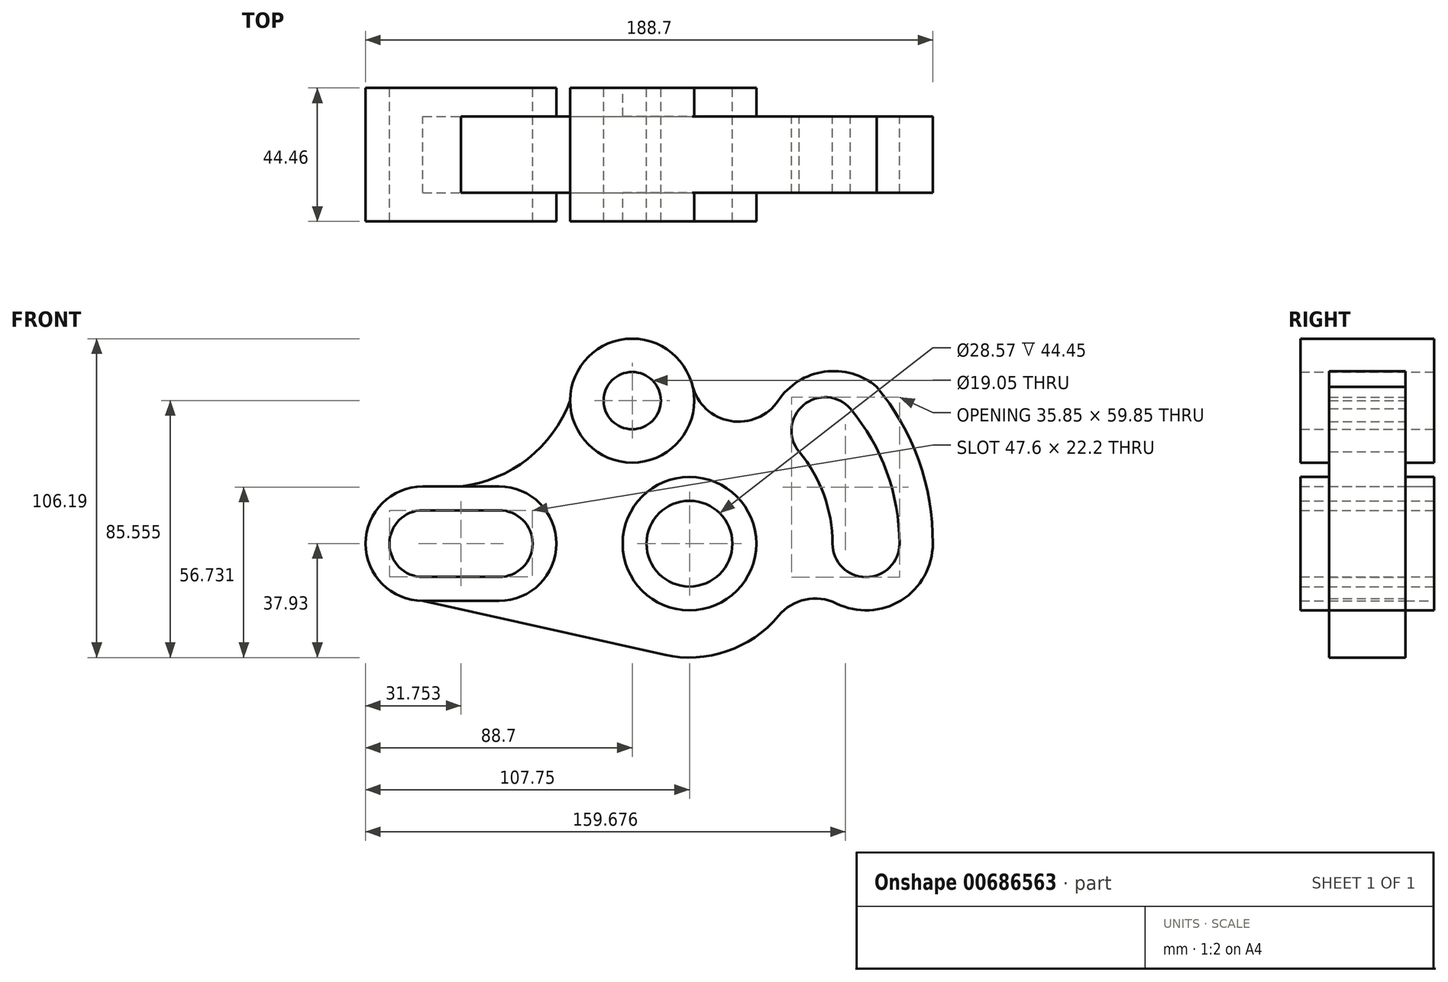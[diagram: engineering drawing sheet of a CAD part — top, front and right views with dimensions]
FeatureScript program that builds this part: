
annotation { "Feature Type Name" : "Feature", "Feature Type Description" : "" }
export const myFeature = defineFeature(function(context is Context, id is Id, definition is map)
    precondition{}
    {
        {
            var Q0;
            Q0=qCreatedBy(makeId("Front.planeOp"),FACE);
            var sketch = newSketch(context, id + "F0", { "sketchPlane" : qUnion([Q0])});
            skCircle(sketch, "E0", {"center": v(0, 0) * mm, "radius": 14.29 * mm});
            skCircle(sketch, "E1", {"center": v(0, 0) * mm, "radius": 22.23 * mm});
            skCircle(sketch, "E2", {"center": v(-19.05, 47.62) * mm, "radius": 9.53 * mm});
            skCircle(sketch, "E3", {"center": v(-19.05, 47.62) * mm, "radius": 20.64 * mm});
            skArc(sketch, "E4", {"start": v(-88.7, 11.1) * mm, "mid": v(-99.8, 0) * mm, "end": v(-88.7, -11.1) * mm});
            skArc(sketch, "E5", {"start": v(-63.3, -11.1) * mm, "mid": v(-52.2, 0) * mm, "end": v(-63.3, 11.1) * mm});
            skLineSegment(sketch, "E6", {"start": v(-88.7, 11.1) * mm, "end": v(-63.3, 11.1) * mm});
            skLineSegment(sketch, "E7", {"start": v(-88.7, -11.1) * mm, "end": v(-63.3, -11.1) * mm});
            skArc(sketch, "E8", {"start": v(48.87, -19.92) * mm, "mid": v(70.45, -18.88) * mm, "end": v(80.95, 0) * mm});
            skLineSegment(sketch, "E9", {"start": v(0, 0) * mm, "end": v(17.03, 14.29) * mm, "construction": true});
            skLineSegment(sketch, "E10", {"start": v(0, 0) * mm, "end": v(22.23, 0) * mm, "construction": true});
            skArc(sketch, "E11.filletArc", {"start": v(48.87, -19.92) * mm, "mid": v(38.53, -18.62) * mm, "end": v(29.62, -24.02) * mm});
            skArc(sketch, "E12", {"start": v(47.6, 0) * mm, "mid": v(58.72, -11.13) * mm, "end": v(69.85, 0) * mm});
            skArc(sketch, "E13", {"start": v(53.5, 44.9) * mm, "mid": v(37.93, 46.16) * mm, "end": v(36.46, 30.6) * mm});
            skArc(sketch, "E14", {"start": v(62.28, 52.26) * mm, "mid": v(44.88, 57.24) * mm, "end": v(29.55, 47.63) * mm});
            skLineSegment(sketch, "E15", {"start": v(0, 0) * mm, "end": v(-125.57, 0) * mm, "construction": true});
            skLineSegment(sketch, "E16", {"start": v(0, 0) * mm, "end": v(0, 0.55) * mm, "construction": true});
            skArc(sketch, "E17", {"start": v(36.46, 30.6) * mm, "mid": v(44.73, 16.28) * mm, "end": v(47.6, 0) * mm});
            skArc(sketch, "E18", {"start": v(53.5, 44.9) * mm, "mid": v(65.64, 23.9) * mm, "end": v(69.85, 0) * mm});
            skArc(sketch, "E19", {"start": v(62.28, 52.26) * mm, "mid": v(76.23, 27.78) * mm, "end": v(80.95, 0) * mm});
            skLineSegment(sketch, "E20.trimOffspring", {"start": v(0, 14.29) * mm, "end": v(0, 22.23) * mm, "construction": true});
            skLineSegment(sketch, "E21.trimOffspring", {"start": v(0, 0.55) * mm, "end": v(0, 0) * mm, "construction": true});
            skLineSegment(sketch, "E22.trimOffspring", {"start": v(0, -14.29) * mm, "end": v(0, -22.23) * mm, "construction": true});
            skArc(sketch, "E23", {"start": v(-63.3, -19.05) * mm, "mid": v(-44.25, 0) * mm, "end": v(-63.3, 19.05) * mm});
            skLineSegment(sketch, "E24", {"start": v(-88.7, 19.05) * mm, "end": v(-63.3, 19.05) * mm});
            skLineSegment(sketch, "E25", {"start": v(-88.7, -19.05) * mm, "end": v(-63.3, -19.05) * mm});
            skLineSegment(sketch, "E26", {"start": v(-76, 0) * mm, "end": v(-76, 19.05) * mm, "construction": true});
            skPoint(sketch, "E26.startSnap0", {"position": v(-76, 11.1) * mm});
            skPoint(sketch, "E26.endSnap0", {"position": v(-76, 19.05) * mm});
            skArc(sketch, "E27.MirrorCS", {"start": v(-88.7, -19.05) * mm, "mid": v(-107.75, 0) * mm, "end": v(-88.7, 19.05) * mm});
            skArc(sketch, "E28", {"start": v(-76, 19.05) * mm, "mid": v(-53.84, 28.25) * mm, "end": v(-39.69, 47.62) * mm});
            skArc(sketch, "E29", {"start": v(-8.4, -37) * mm, "mid": v(12.44, -35.86) * mm, "end": v(29.62, -24.02) * mm});
            skLineSegment(sketch, "E30", {"start": v(-88.7, -19.05) * mm, "end": v(-8.4, -37) * mm});
            skArc(sketch, "E31", {"start": v(0.97, 52.63) * mm, "mid": v(13.64, 40.84) * mm, "end": v(29.55, 47.62) * mm});
            skPoint(sketch, "E32.orphan", {"position": v(-76, 37.27) * mm});
            skLineSegment(sketch, "E33.trimOffspring", {"start": v(62.28, 52.26) * mm, "end": v(90.16, 75.27) * mm, "construction": true});
            skLineSegment(sketch, "E34.trimOffspring", {"start": v(80.95, 0) * mm, "end": v(110.19, 0) * mm, "construction": true});
            skSolve(sketch);
        }
        {
            var Q0;
            Q0=makeQuery(id+"F0.imprint","IMPRINT",FACE,{"disambiguationData":[TD([[makeQuery(id+"F0.imprint","IMPRINT",EDGE,{"derivedFrom":sQuery(id+"F0.wireOp",EDGE,"E1")}),-1.0]])]});
            extrude(context, id + "F1", {"entities" : qUnion([Q0]), "endBound" : BoundingType.SYMMETRIC, "depth" : 25.4 * mm, "offsetDistance" : 25.4 * mm});
        }
        {
            var Q0;
            Q0=makeQuery(id+"F0.imprint","IMPRINT",FACE,{"disambiguationData":[TD([[makeQuery(id+"F0.imprint","IMPRINT",EDGE,{"derivedFrom":sQuery(id+"F0.wireOp",EDGE,"E0")}),-1.0]])]});
            var Q1;
            Q1=makeQuery(id+"F0.imprint","IMPRINT",FACE,{"disambiguationData":[TD([[makeQuery(id+"F0.imprint","IMPRINT",EDGE,{"derivedFrom":sQuery(id+"F0.wireOp",EDGE,"E4")}),-1.0]])]});
            var Q2;
            Q2=makeQuery(id+"F0.imprint","IMPRINT",FACE,{"disambiguationData":[TD([[makeQuery(id+"F0.imprint","IMPRINT",EDGE,{"derivedFrom":sQuery(id+"F0.wireOp",EDGE,"E2")}),-1.0]])]});
            extrude(context, id + "F2", {"entities" : qUnion([Q0, Q1, Q2]), "operationType" : NewBodyOperationType.ADD, "endBound" : BoundingType.SYMMETRIC, "depth" : 44.45 * mm, "offsetDistance" : 25.4 * mm});
        }
    });
